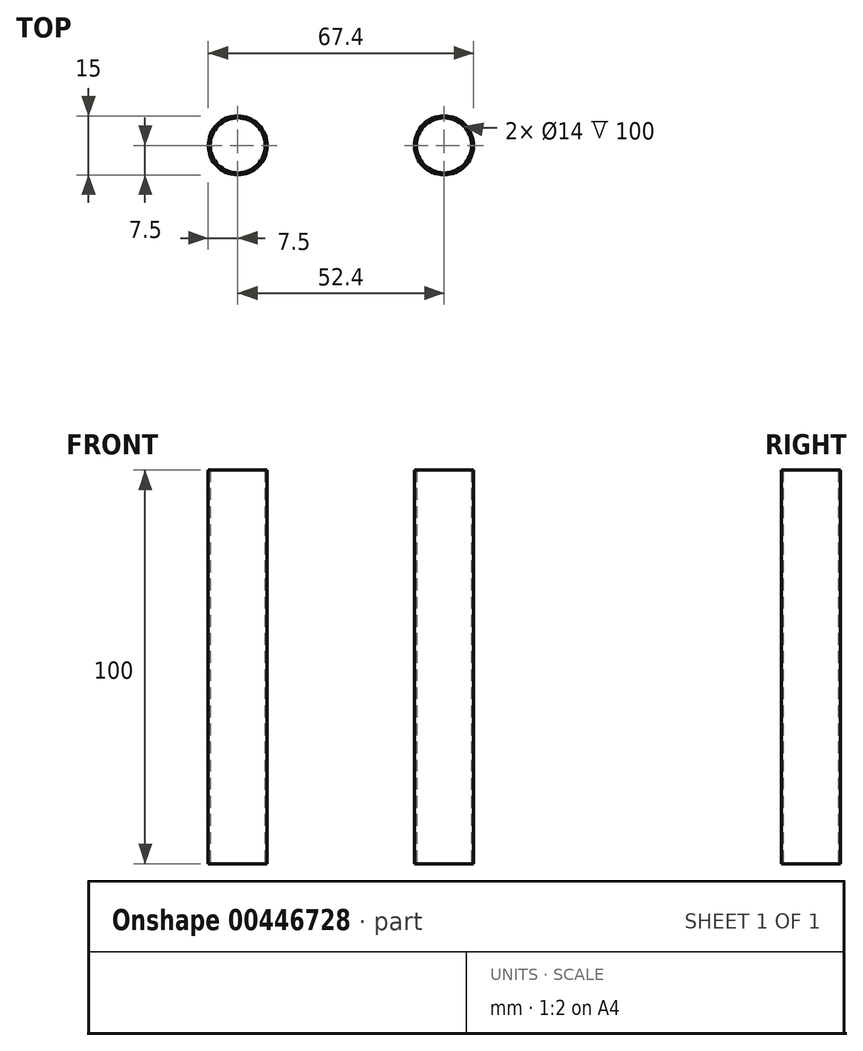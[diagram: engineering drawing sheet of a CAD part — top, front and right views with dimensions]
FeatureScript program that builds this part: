
annotation { "Feature Type Name" : "Feature", "Feature Type Description" : "" }
export const myFeature = defineFeature(function(context is Context, id is Id, definition is map)
    precondition{}
    {
        {
            var Q0;
            Q0=qCreatedBy(makeId("Top.planeOp"),FACE);
            var sketch = newSketch(context, id + "F0", { "sketchPlane" : qUnion([Q0])});
            skCircle(sketch, "E0", {"center": v(-26.2, 0) * mm, "radius": 7.5 * mm});
            skCircle(sketch, "E1", {"center": v(26.2, 0) * mm, "radius": 7.5 * mm});
            skLineSegment(sketch, "E2", {"start": v(0, 27.15) * mm, "end": v(0, -30.16) * mm});
            skCircle(sketch, "E3", {"center": v(-26.2, 0) * mm, "radius": 7 * mm});
            skCircle(sketch, "E4", {"center": v(26.2, 0) * mm, "radius": 7 * mm});
            skSolve(sketch);
        }
        {
            var Q0;
            Q0 = qSketchRegion(id + "F0", true);
            extrude(context, id + "F1", {"entities" : qUnion([Q0]), "endBound" : BoundingType.SYMMETRIC, "depth" : 100 * mm});
        }
    });
